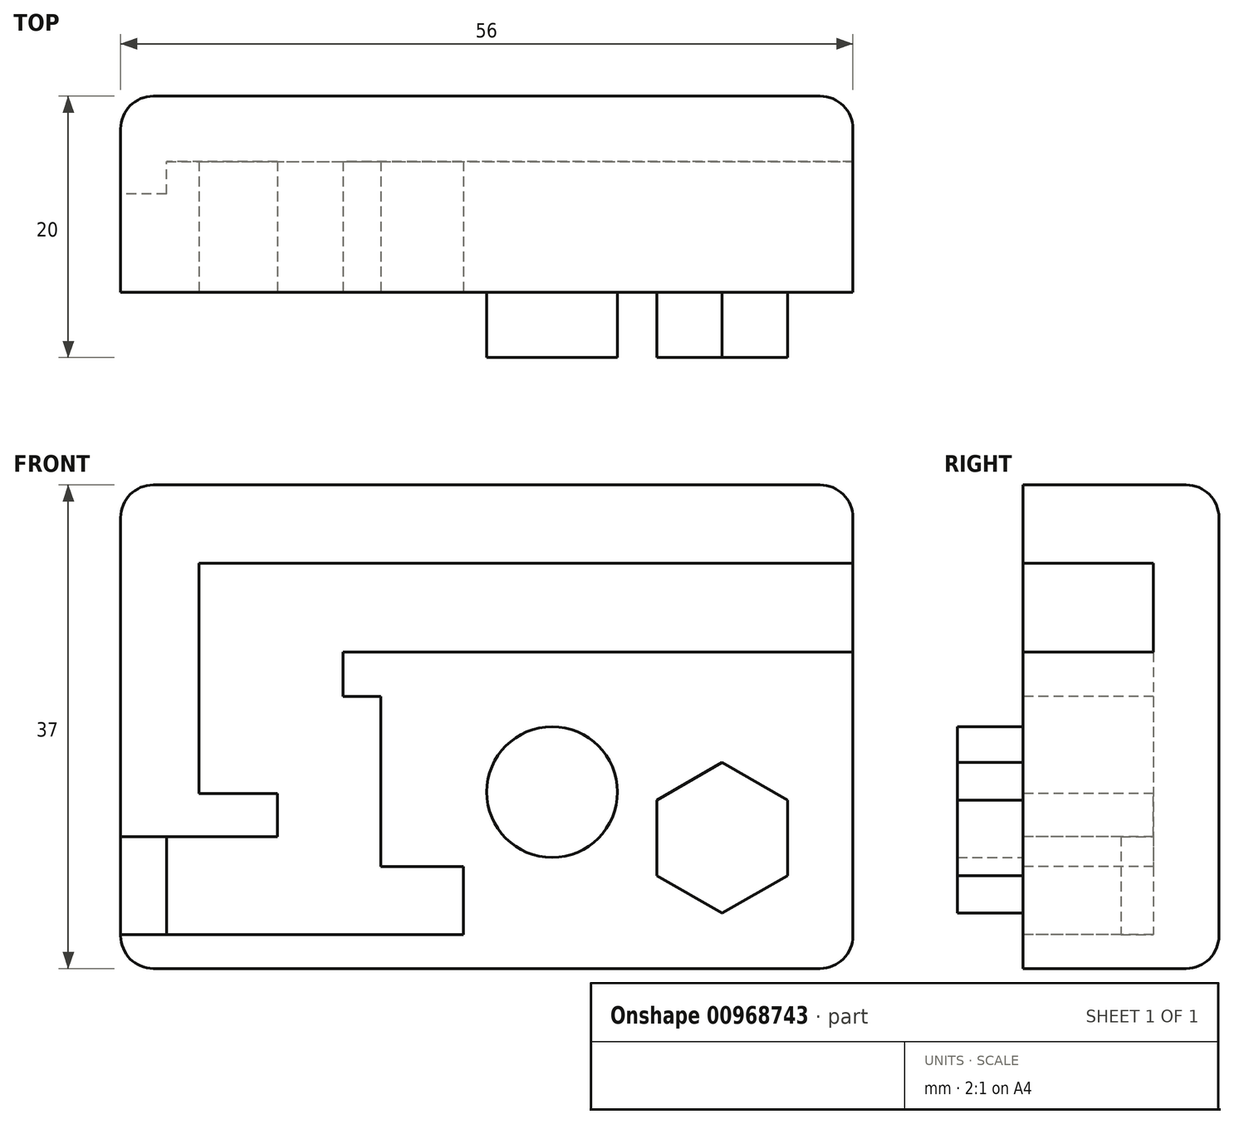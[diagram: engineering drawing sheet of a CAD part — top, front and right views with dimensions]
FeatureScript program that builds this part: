
annotation { "Feature Type Name" : "Feature", "Feature Type Description" : "" }
export const myFeature = defineFeature(function(context is Context, id is Id, definition is map)
    precondition{}
    {
        {
            var Q0;
            Q0=qCreatedBy(makeId("Front.planeOp"),FACE);
            var sketch = newSketch(context, id + "F0", { "sketchPlane" : qUnion([Q0])});
            skLineSegment(sketch, "E0.bottom", {"start": v(-24.5, 18.5) * mm, "end": v(24.5, 18.5) * mm});
            skLineSegment(sketch, "E0.top", {"start": v(-24.5, -18.5) * mm, "end": v(24.5, -18.5) * mm});
            skLineSegment(sketch, "E1", {"start": v(24.5, 18.5) * mm, "end": v(28, 18.5) * mm});
            skLineSegment(sketch, "E2", {"start": v(28, 18.5) * mm, "end": v(28, -18.5) * mm});
            skLineSegment(sketch, "E3", {"start": v(28, -18.5) * mm, "end": v(24.5, -18.5) * mm});
            skLineSegment(sketch, "E4", {"start": v(-24.5, 18.5) * mm, "end": v(-28, 18.5) * mm});
            skLineSegment(sketch, "E5", {"start": v(-28, 18.5) * mm, "end": v(-28, -18.5) * mm});
            skLineSegment(sketch, "E6", {"start": v(-28, -18.5) * mm, "end": v(-24.5, -18.5) * mm});
            skSolve(sketch);
        }
        {
            var Q0;
            Q0 = qSketchRegion(id + "F0", true);
            extrude(context, id + "F1", {"entities" : qUnion([Q0]), "depth" : 15 * mm, "offsetDistance" : 25 * mm});
        }
        {
            var Q0;
            Q0=makeQuery(id+"F1.opExtrude","CAP_FACE",FACE,{"disambiguationData":[OSD([sQuery(id+"F0.wireOp",EDGE,"E0.bottom"),sQuery(id+"F0.wireOp",EDGE,"E0.top"),sQuery(id+"F0.wireOp",EDGE,"E0.left"),sQuery(id+"F0.wireOp",EDGE,"E0.right")])],"isStart":false});
            var sketch = newSketch(context, id + "F2", { "sketchPlane" : qUnion([Q0])});
            skLineSegment(sketch, "E7", {"start": v(24.5, 12.5) * mm, "end": v(-22, 12.5) * mm});
            skLineSegment(sketch, "E8", {"start": v(-22, 12.5) * mm, "end": v(-22, -5.1) * mm});
            skLineSegment(sketch, "E9", {"start": v(-22, -5.1) * mm, "end": v(-16, -5.1) * mm});
            skLineSegment(sketch, "E10", {"start": v(-16, -8.4) * mm, "end": v(-16, -5.1) * mm});
            skLineSegment(sketch, "E11", {"start": v(-16, -8.4) * mm, "end": v(-24.5, -8.4) * mm});
            skLineSegment(sketch, "E12", {"start": v(24.5, 5.7) * mm, "end": v(-11, 5.7) * mm});
            skLineSegment(sketch, "E13", {"start": v(-11, 2.3) * mm, "end": v(-8.1, 2.3) * mm});
            skLineSegment(sketch, "E14", {"start": v(-8.1, 2.3) * mm, "end": v(-8.1, -10.7) * mm});
            skLineSegment(sketch, "E15", {"start": v(-8.1, -10.7) * mm, "end": v(-1.8, -10.7) * mm});
            skLineSegment(sketch, "E16", {"start": v(-24.5, -15.9) * mm, "end": v(-1.8, -15.9) * mm});
            skLineSegment(sketch, "E17", {"start": v(-1.8, -10.7) * mm, "end": v(-1.8, -15.9) * mm});
            skLineSegment(sketch, "E18", {"start": v(28, 12.5) * mm, "end": v(28, 5.7) * mm});
            skLineSegment(sketch, "E19", {"start": v(-24.5, -8.4) * mm, "end": v(-28, -8.4) * mm});
            skLineSegment(sketch, "E20", {"start": v(-28, -8.4) * mm, "end": v(-28, -15.9) * mm});
            skLineSegment(sketch, "E21", {"start": v(-28, -15.9) * mm, "end": v(-24.5, -15.9) * mm});
            skLineSegment(sketch, "E22", {"start": v(24.5, 12.5) * mm, "end": v(28, 12.5) * mm});
            skLineSegment(sketch, "E23", {"start": v(28, 5.7) * mm, "end": v(24.5, 5.7) * mm});
            skLineSegment(sketch, "E24", {"start": v(-11, 5.7) * mm, "end": v(-11, 2.3) * mm});
            skSolve(sketch);
        }
        {
            var Q0;
            Q0=makeQuery(id+"F2.imprint","IMPRINT",FACE,{"disambiguationData":[TD([[makeQuery(id+"F2.imprint","IMPRINT",EDGE,{"derivedFrom":sQuery(id+"F2.wireOp",EDGE,"E7")}),1.0]])]});
            extrude(context, id + "F3", {"entities" : qUnion([Q0]), "operationType" : NewBodyOperationType.REMOVE, "oppositeDirection" : true, "depth" : 10 * mm, "offsetDistance" : 25 * mm});
        }
        {
            var Q0;
            {var subQ0=sQuery(id+"F0.wireOp",EDGE,"E5");var subQ1=sQuery(id+"F0.wireOp",EDGE,"E2");var subQ2=sQuery(id+"F0.wireOp",EDGE,"E4");var subQ3=sQuery(id+"F0.wireOp",EDGE,"E1");var subQ4=sQuery(id+"F0.wireOp",EDGE,"E0.bottom");Q0=makeQuery(id+"F3.boolean.opBoolean","SPLIT",FACE,{"disambiguationData":[TD([makeQuery(id+"F3.opExtrude","SWEPT_FACE",FACE,{"disambiguationData":[OSD([sQuery(id+"F2.wireOp",EDGE,"E8")])]})])],"derivedFrom":makeQuery(id+"F1.opExtrude","CAP_FACE",FACE,{"disambiguationData":[OSD([subQ4,sQuery(id+"F0.wireOp",EDGE,"E0.top"),subQ3,subQ1,sQuery(id+"F0.wireOp",EDGE,"E3"),subQ2,subQ0,sQuery(id+"F0.wireOp",EDGE,"E6")])],"isStart":false})});}
            var sketch = newSketch(context, id + "F4", { "sketchPlane" : qUnion([Q0])});
            skCircle(sketch, "E25.cCircle", {"center": v(18, -8.5) * mm, "radius": 5 * mm, "construction": true});
            skLineSegment(sketch, "E25.0", {"start": v(23, -5.61) * mm, "end": v(23, -11.39) * mm});
            skLineSegment(sketch, "E25.1", {"start": v(23, -11.39) * mm, "end": v(18, -14.27) * mm});
            skLineSegment(sketch, "E25.2", {"start": v(18, -14.27) * mm, "end": v(13, -11.39) * mm});
            skLineSegment(sketch, "E25.3", {"start": v(13, -11.39) * mm, "end": v(13, -5.61) * mm});
            skLineSegment(sketch, "E25.4", {"start": v(13, -5.61) * mm, "end": v(18, -2.73) * mm});
            skLineSegment(sketch, "E25.5", {"start": v(18, -2.73) * mm, "end": v(23, -5.61) * mm});
            skPoint(sketch, "E25.0.midPoint", {"position": v(23, -8.5) * mm});
            skSolve(sketch);
        }
        {
            var Q0;
            Q0 = qSketchRegion(id + "F4", true);
            extrude(context, id + "F5", {"entities" : qUnion([Q0]), "operationType" : NewBodyOperationType.ADD, "depth" : 5 * mm, "offsetDistance" : 25 * mm});
        }
        {
            var Q0;
            Q0=makeQuery(id+"F3.boolean.opBoolean","COPY",FACE,{"derivedFrom":makeQuery(id+"F3.opExtrude","CAP_FACE",FACE,{"disambiguationData":[OSD([sQuery(id+"F2.wireOp",EDGE,"E7"),sQuery(id+"F2.wireOp",EDGE,"E8"),sQuery(id+"F2.wireOp",EDGE,"E9"),sQuery(id+"F2.wireOp",EDGE,"E10"),sQuery(id+"F2.wireOp",EDGE,"E11"),sQuery(id+"F2.wireOp",EDGE,"E12"),sQuery(id+"F2.wireOp",EDGE,"E13"),sQuery(id+"F2.wireOp",EDGE,"E14"),sQuery(id+"F2.wireOp",EDGE,"E15"),sQuery(id+"F2.wireOp",EDGE,"E16"),sQuery(id+"F2.wireOp",EDGE,"E17"),sQuery(id+"F2.wireOp",EDGE,"E18"),sQuery(id+"F2.wireOp",EDGE,"E19"),sQuery(id+"F2.wireOp",EDGE,"E20"),sQuery(id+"F2.wireOp",EDGE,"E21"),sQuery(id+"F2.wireOp",EDGE,"E22"),sQuery(id+"F2.wireOp",EDGE,"E23"),sQuery(id+"F2.wireOp",EDGE,"E24")])],"isStart":false})});
            var sketch = newSketch(context, id + "F6", { "sketchPlane" : qUnion([Q0])});
            skLineSegment(sketch, "E26.bottom", {"start": v(-28, -8.4) * mm, "end": v(-24.5, -8.4) * mm});
            skLineSegment(sketch, "E26.top", {"start": v(-28, -15.9) * mm, "end": v(-24.5, -15.9) * mm});
            skLineSegment(sketch, "E26.left", {"start": v(-28, -8.4) * mm, "end": v(-28, -15.9) * mm});
            skLineSegment(sketch, "E26.right", {"start": v(-24.5, -8.4) * mm, "end": v(-24.5, -15.9) * mm});
            skSolve(sketch);
        }
        {
            var Q0;
            Q0 = qSketchRegion(id + "F6", true);
            extrude(context, id + "F7", {"entities" : qUnion([Q0]), "operationType" : NewBodyOperationType.ADD, "depth" : 2.5 * mm, "offsetDistance" : 25 * mm});
        }
        {
            var Q0;
            Q0=makeQuery(id+"F1.opExtrude","SWEPT_EDGE",EDGE,{"disambiguationData":[OSD([sQuery(id+"F0.wireOp",EDGE,"E4"),sQuery(id+"F0.wireOp",EDGE,"E5")])]});
            var Q1;
            Q1=makeQuery(id+"F1.opExtrude","SWEPT_EDGE",EDGE,{"disambiguationData":[OSD([sQuery(id+"F0.wireOp",EDGE,"E1"),sQuery(id+"F0.wireOp",EDGE,"E2")])]});
            var Q2;
            Q2=makeQuery(id+"F1.opExtrude","SWEPT_EDGE",EDGE,{"disambiguationData":[OSD([sQuery(id+"F0.wireOp",EDGE,"E2"),sQuery(id+"F0.wireOp",EDGE,"E3")])]});
            var Q3;
            Q3=makeQuery(id+"F1.opExtrude","SWEPT_EDGE",EDGE,{"disambiguationData":[OSD([sQuery(id+"F0.wireOp",EDGE,"E5"),sQuery(id+"F0.wireOp",EDGE,"E6")])]});
            var Q4;
            Q4=makeQuery(id+"F1.opExtrude","CAP_EDGE",EDGE,{"disambiguationData":[OSD([sQuery(id+"F0.wireOp",EDGE,"E0.top"),sQuery(id+"F0.wireOp",EDGE,"E3"),sQuery(id+"F0.wireOp",EDGE,"E6")])],"isStart":true});
            var Q5;
            Q5=makeQuery(id+"F1.opExtrude","CAP_FACE",FACE,{"disambiguationData":[OSD([sQuery(id+"F0.wireOp",EDGE,"E0.bottom"),sQuery(id+"F0.wireOp",EDGE,"E0.top"),sQuery(id+"F0.wireOp",EDGE,"E1"),sQuery(id+"F0.wireOp",EDGE,"E2"),sQuery(id+"F0.wireOp",EDGE,"E3"),sQuery(id+"F0.wireOp",EDGE,"E4"),sQuery(id+"F0.wireOp",EDGE,"E5"),sQuery(id+"F0.wireOp",EDGE,"E6")])],"isStart":true});
            fillet(context, id + "F8", {"entities" : qUnion([Q0, Q1, Q2, Q3, Q4, Q5]), "radius" : 2.5 * mm, "tangentPropagation" : true, "allowEdgeOverflow" : false});
        }
        {
            var Q0;
            {var subQ0=sQuery(id+"F0.wireOp",EDGE,"E5");var subQ1=sQuery(id+"F0.wireOp",EDGE,"E2");var subQ2=sQuery(id+"F0.wireOp",EDGE,"E6");var subQ3=sQuery(id+"F0.wireOp",EDGE,"E3");var subQ4=sQuery(id+"F0.wireOp",EDGE,"E0.top");Q0=makeQuery(id+"F3.boolean.opBoolean","SPLIT",FACE,{"disambiguationData":[TD([makeQuery(id+"F3.opExtrude","SWEPT_FACE",FACE,{"disambiguationData":[OSD([sQuery(id+"F2.wireOp",EDGE,"E13")])]})])],"derivedFrom":makeQuery(id+"F1.opExtrude","CAP_FACE",FACE,{"disambiguationData":[OSD([sQuery(id+"F0.wireOp",EDGE,"E0.bottom"),subQ4,sQuery(id+"F0.wireOp",EDGE,"E1"),subQ1,subQ3,sQuery(id+"F0.wireOp",EDGE,"E4"),subQ0,subQ2])],"isStart":false})});}
            var sketch = newSketch(context, id + "F9", { "sketchPlane" : qUnion([Q0])});
            skCircle(sketch, "E27", {"center": v(5, -5) * mm, "radius": 5 * mm});
            skSolve(sketch);
        }
        {
            var Q0;
            Q0 = qSketchRegion(id + "F9", true);
            extrude(context, id + "F10", {"entities" : qUnion([Q0]), "operationType" : NewBodyOperationType.ADD, "depth" : 5 * mm, "offsetDistance" : 25 * mm});
        }
    });
